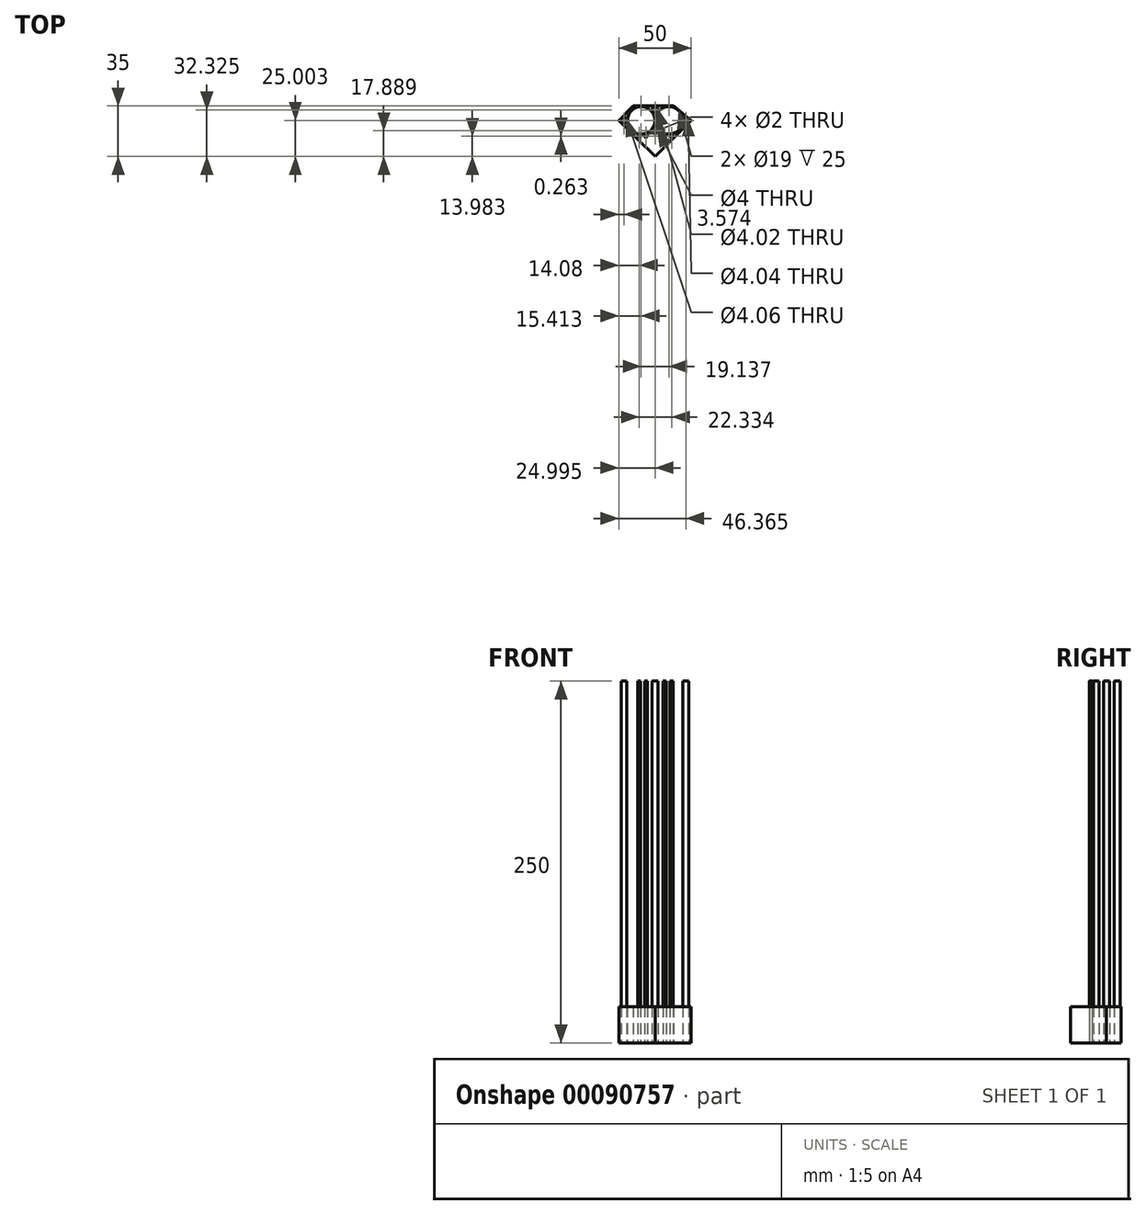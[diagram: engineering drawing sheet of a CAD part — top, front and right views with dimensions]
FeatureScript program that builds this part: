
annotation { "Feature Type Name" : "Feature", "Feature Type Description" : "" }
export const myFeature = defineFeature(function(context is Context, id is Id, definition is map)
    precondition{}
    {
        {
            var Q0;
            Q0=qCreatedBy(makeId("Top.planeOp"),FACE);
            var sketch = newSketch(context, id + "F0", { "sketchPlane" : qUnion([Q0])});
            skLineSegment(sketch, "E0.bottom", {"start": v(116.29, -55.55) * mm, "end": v(66.29, -55.55) * mm, "construction": true});
            skLineSegment(sketch, "E0.top", {"start": v(116.29, -105.55) * mm, "end": v(66.29, -105.55) * mm, "construction": true});
            skLineSegment(sketch, "E0.left", {"start": v(116.29, -55.55) * mm, "end": v(116.29, -105.55) * mm, "construction": true});
            skLineSegment(sketch, "E0.right", {"start": v(66.29, -55.55) * mm, "end": v(66.29, -105.55) * mm, "construction": true});
            skPoint(sketch, "E0.middle", {"position": v(91.29, -80.55) * mm});
            skLineSegment(sketch, "E1", {"start": v(91.29, -80.55) * mm, "end": v(66.29, -55.55) * mm, "construction": true});
            skLineSegment(sketch, "E2", {"start": v(91.29, -80.55) * mm, "end": v(116.29, -55.55) * mm, "construction": true});
            skLineSegment(sketch, "E3", {"start": v(66.29, -55.55) * mm, "end": v(76.29, -45.55) * mm, "construction": true});
            skLineSegment(sketch, "E4", {"start": v(76.29, -45.55) * mm, "end": v(104.27, -45.55) * mm, "construction": true});
            skLineSegment(sketch, "E5", {"start": v(104.27, -45.55) * mm, "end": v(116.29, -55.55) * mm, "construction": true});
            skLineSegment(sketch, "E6.bottom", {"start": v(95.9, -8.57) * mm, "end": v(117.9, -8.57) * mm});
            skLineSegment(sketch, "E6.top", {"start": v(95.9, 6.45) * mm, "end": v(117.9, 6.45) * mm});
            skLineSegment(sketch, "E6.left", {"start": v(95.9, -8.57) * mm, "end": v(95.9, 6.45) * mm});
            skLineSegment(sketch, "E6.right", {"start": v(117.9, -8.57) * mm, "end": v(117.9, 6.45) * mm});
            skLineSegment(sketch, "E7", {"start": v(91.29, -80.55) * mm, "end": v(91.29, -12.55) * mm, "construction": true});
            skCircle(sketch, "E8", {"center": v(81.7, -55.55) * mm, "radius": 9.5 * mm});
            skCircle(sketch, "E9", {"center": v(100.84, -55.55) * mm, "radius": 9.5 * mm});
            skCircle(sketch, "E10", {"center": v(69.86, -55.55) * mm, "radius": 2.03 * mm});
            skCircle(sketch, "E11", {"center": v(112.65, -55.55) * mm, "radius": 2.02 * mm});
            skLineSegment(sketch, "E12", {"start": v(78.79, -68.05) * mm, "end": v(103.79, -68.05) * mm});
            skCircle(sketch, "E13", {"center": v(91.29, -62.66) * mm, "radius": 2 * mm});
            skCircle(sketch, "E14", {"center": v(91.29, -48.23) * mm, "radius": 2.01 * mm});
            skCircle(sketch, "E15", {"center": v(91.29, -71.4) * mm, "radius": 6.08 * mm});
            skCircle(sketch, "E16", {"center": v(97.97, -66.4) * mm, "radius": 1 * mm});
            skCircle(sketch, "E17", {"center": v(85.01, -66.3) * mm, "radius": 1 * mm});
            skCircle(sketch, "E18", {"center": v(80.37, -66.57) * mm, "radius": 1 * mm});
            skCircle(sketch, "E19", {"center": v(102.7, -66.48) * mm, "radius": 1 * mm});
            skCircle(sketch, "E20", {"center": v(109.19, -76.46) * mm, "radius": 1.25 * mm});
            skSolve(sketch);
        }
        {
            var Q0;
            Q0=makeQuery(id+"F0.imprint","IMPRINT",FACE,{"disambiguationData":[TD([[makeQuery(id+"F0.imprint","IMPRINT",EDGE,{"derivedFrom":sQuery(id+"F0.wireOp",EDGE,"E14")}),1.0]])]});
            var Q1;
            Q1=makeQuery(id+"F0.imprint","IMPRINT",FACE,{"disambiguationData":[TD([[makeQuery(id+"F0.imprint","IMPRINT",EDGE,{"derivedFrom":sQuery(id+"F0.wireOp",EDGE,"E11")}),1.0]])]});
            var Q2;
            Q2=makeQuery(id+"F0.imprint","IMPRINT",FACE,{"disambiguationData":[TD([[makeQuery(id+"F0.imprint","IMPRINT",EDGE,{"derivedFrom":sQuery(id+"F0.wireOp",EDGE,"E19")}),1.0]])]});
            var Q3;
            Q3=makeQuery(id+"F0.imprint","IMPRINT",FACE,{"disambiguationData":[TD([[makeQuery(id+"F0.imprint","IMPRINT",EDGE,{"derivedFrom":sQuery(id+"F0.wireOp",EDGE,"E16")}),1.0]])]});
            var Q4;
            Q4=makeQuery(id+"F0.imprint","IMPRINT",FACE,{"disambiguationData":[TD([[makeQuery(id+"F0.imprint","IMPRINT",EDGE,{"derivedFrom":sQuery(id+"F0.wireOp",EDGE,"E13")}),1.0]])]});
            var Q5;
            Q5=makeQuery(id+"F0.imprint","IMPRINT",FACE,{"disambiguationData":[TD([[makeQuery(id+"F0.imprint","IMPRINT",EDGE,{"derivedFrom":sQuery(id+"F0.wireOp",EDGE,"E17")}),1.0]])]});
            var Q6;
            Q6=makeQuery(id+"F0.imprint","IMPRINT",FACE,{"disambiguationData":[TD([[makeQuery(id+"F0.imprint","IMPRINT",EDGE,{"derivedFrom":sQuery(id+"F0.wireOp",EDGE,"E18")}),1.0]])]});
            var Q7;
            Q7=makeQuery(id+"F0.imprint","IMPRINT",FACE,{"disambiguationData":[TD([[makeQuery(id+"F0.imprint","IMPRINT",EDGE,{"derivedFrom":sQuery(id+"F0.wireOp",EDGE,"E10")}),1.0]])]});
            extrude(context, id + "F1", {"entities" : qUnion([Q0, Q1, Q2, Q3, Q4, Q5, Q6, Q7]), "depth" : 250 * mm});
        }
        {
            var Q0;
            Q0=qCreatedBy(makeId("Top.planeOp"),FACE);
            var sketch = newSketch(context, id + "F2", { "sketchPlane" : qUnion([Q0])});
            skCircle(sketch, "E21.0", {"center": v(80.37, -66.57) * mm, "radius": 1 * mm});
            skCircle(sketch, "E21.1", {"center": v(91.29, -62.66) * mm, "radius": 2 * mm});
            skCircle(sketch, "E21.2", {"center": v(112.65, -55.55) * mm, "radius": 2.02 * mm});
            skCircle(sketch, "E21.3", {"center": v(81.7, -55.55) * mm, "radius": 9.5 * mm});
            skCircle(sketch, "E21.4", {"center": v(100.84, -55.55) * mm, "radius": 9.5 * mm});
            skLineSegment(sketch, "E21.5", {"start": v(116.29, -55.55) * mm, "end": v(66.29, -55.55) * mm});
            skLineSegment(sketch, "E21.6", {"start": v(66.29, -55.55) * mm, "end": v(76.29, -45.55) * mm});
            skLineSegment(sketch, "E21.7", {"start": v(76.29, -45.55) * mm, "end": v(104.27, -45.55) * mm});
            skLineSegment(sketch, "E21.8", {"start": v(104.27, -45.55) * mm, "end": v(116.29, -55.55) * mm});
            skCircle(sketch, "E21.9", {"center": v(102.7, -66.48) * mm, "radius": 1 * mm});
            skCircle(sketch, "E21.10", {"center": v(85.01, -66.3) * mm, "radius": 1 * mm});
            skCircle(sketch, "E21.11", {"center": v(97.97, -66.4) * mm, "radius": 1 * mm});
            skCircle(sketch, "E21.12", {"center": v(91.29, -48.23) * mm, "radius": 2.01 * mm});
            skLineSegment(sketch, "E21.13", {"start": v(78.79, -68.05) * mm, "end": v(103.79, -68.05) * mm});
            skCircle(sketch, "E21.14", {"center": v(69.86, -55.55) * mm, "radius": 2.03 * mm});
            skCircle(sketch, "E21.15", {"center": v(91.29, -48.23) * mm, "radius": 2.01 * mm});
            skCircle(sketch, "E21.16", {"center": v(91.29, -62.66) * mm, "radius": 2 * mm});
            skCircle(sketch, "E21.17", {"center": v(112.65, -55.55) * mm, "radius": 2.02 * mm});
            skCircle(sketch, "E21.18", {"center": v(69.86, -55.55) * mm, "radius": 2.03 * mm});
            skCircle(sketch, "E21.19", {"center": v(102.7, -66.48) * mm, "radius": 1 * mm});
            skCircle(sketch, "E21.20", {"center": v(80.37, -66.57) * mm, "radius": 1 * mm});
            skCircle(sketch, "E21.21", {"center": v(85.01, -66.3) * mm, "radius": 1 * mm});
            skCircle(sketch, "E21.22", {"center": v(97.97, -66.4) * mm, "radius": 1 * mm});
            skCircle(sketch, "E21.23", {"center": v(91.29, -48.23) * mm, "radius": 2.01 * mm});
            skCircle(sketch, "E21.24", {"center": v(91.29, -62.66) * mm, "radius": 2 * mm});
            skCircle(sketch, "E21.25", {"center": v(112.65, -55.55) * mm, "radius": 2.02 * mm});
            skCircle(sketch, "E21.26", {"center": v(69.86, -55.55) * mm, "radius": 2.03 * mm});
            skCircle(sketch, "E21.27", {"center": v(102.7, -66.48) * mm, "radius": 1 * mm});
            skCircle(sketch, "E21.28", {"center": v(80.37, -66.57) * mm, "radius": 1 * mm});
            skCircle(sketch, "E21.29", {"center": v(85.01, -66.3) * mm, "radius": 1 * mm});
            skCircle(sketch, "E21.30", {"center": v(97.97, -66.4) * mm, "radius": 1 * mm});
            skLineSegment(sketch, "E22", {"start": v(116.29, -55.55) * mm, "end": v(103.79, -68.05) * mm});
            skLineSegment(sketch, "E23", {"start": v(78.79, -68.05) * mm, "end": v(66.29, -55.55) * mm});
            skLineSegment(sketch, "E24", {"start": v(103.79, -68.05) * mm, "end": v(91.31, -80.55) * mm});
            skLineSegment(sketch, "E25", {"start": v(91.31, -80.55) * mm, "end": v(78.79, -68.05) * mm});
            skSolve(sketch);
        }
        {
            var Q0;
            Q0 = qSketchRegion(id + "F2", true);
            extrude(context, id + "F3", {"entities" : qUnion([Q0]), "depth" : 25 * mm});
        }
    });
